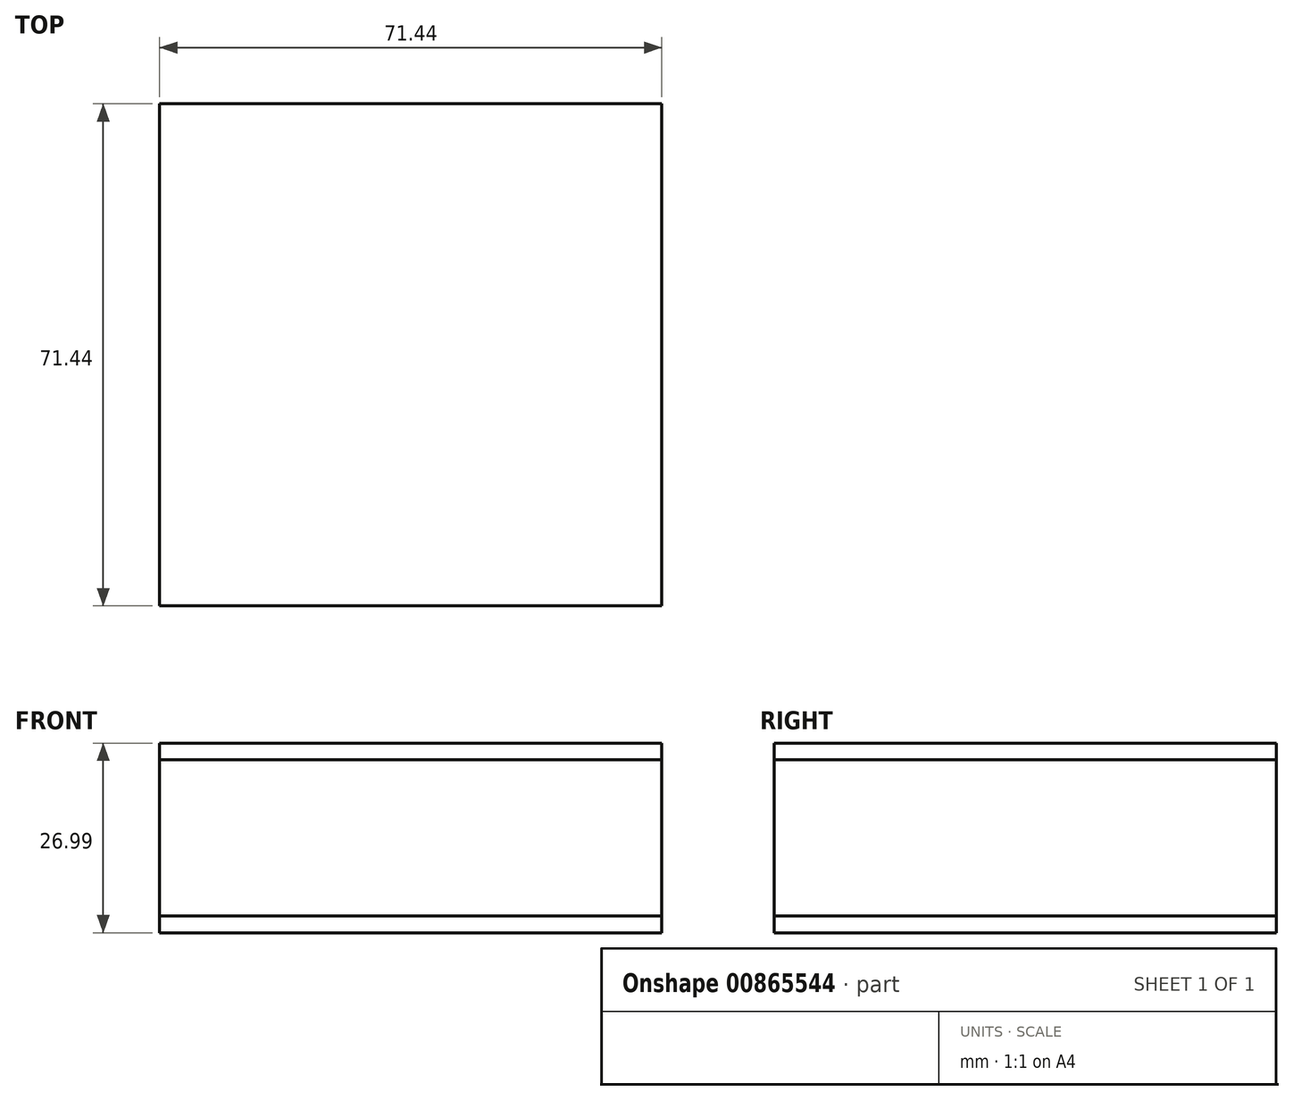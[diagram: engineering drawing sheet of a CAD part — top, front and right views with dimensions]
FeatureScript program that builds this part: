
annotation { "Feature Type Name" : "Feature", "Feature Type Description" : "" }
export const myFeature = defineFeature(function(context is Context, id is Id, definition is map)
    precondition{}
    {
        {
            var Q0;
            Q0=qCreatedBy(makeId("Front.planeOp"),FACE);
            var sketch = newSketch(context, id + "F0", { "sketchPlane" : qUnion([Q0])});
            skLineSegment(sketch, "E0.bottom", {"start": v(0, 0) * mm, "end": v(71.44, 0) * mm});
            skLineSegment(sketch, "E0.top", {"start": v(0, 22.23) * mm, "end": v(71.44, 22.23) * mm});
            skLineSegment(sketch, "E0.left", {"start": v(0, 0) * mm, "end": v(0, 22.23) * mm});
            skLineSegment(sketch, "E0.right", {"start": v(71.44, 0) * mm, "end": v(71.44, 22.23) * mm});
            skSolve(sketch);
        }
        {
            var Q0;
            Q0=makeQuery(id+"F0.imprint","IMPRINT",FACE,{"disambiguationData":[TD([[makeQuery(id+"F0.imprint","IMPRINT",EDGE,{"derivedFrom":sQuery(id+"F0.wireOp",EDGE,"E0.bottom")}),1.0]])]});
            extrude(context, id + "F1", {"entities" : qUnion([Q0]), "depth" : 71.44 * mm, "offsetDistance" : 25.4 * mm});
        }
        {
            var Q0;
            Q0=qCreatedBy(makeId("Front.planeOp"),FACE);
            var sketch = newSketch(context, id + "F2", { "sketchPlane" : qUnion([Q0])});
            skLineSegment(sketch, "E1.bottom", {"start": v(0, 22.23) * mm, "end": v(71.44, 22.23) * mm});
            skLineSegment(sketch, "E1.top", {"start": v(0, 24.6) * mm, "end": v(71.44, 24.6) * mm});
            skLineSegment(sketch, "E1.left", {"start": v(0, 22.23) * mm, "end": v(0, 24.6) * mm});
            skLineSegment(sketch, "E1.right", {"start": v(71.44, 22.23) * mm, "end": v(71.44, 24.6) * mm});
            skLineSegment(sketch, "E2", {"start": v(0, 11.11) * mm, "end": v(71.48, 11.11) * mm, "construction": true});
            skLineSegment(sketch, "E3.MirrorCS", {"start": v(0, 0) * mm, "end": v(71.44, 0) * mm});
            skLineSegment(sketch, "E4.MirrorCS", {"start": v(0, -2.38) * mm, "end": v(71.44, -2.38) * mm});
            skLineSegment(sketch, "E5.MirrorCS", {"start": v(0, 0) * mm, "end": v(0, -2.38) * mm});
            skLineSegment(sketch, "E6.MirrorCS", {"start": v(71.44, 0) * mm, "end": v(71.44, -2.38) * mm});
            skSolve(sketch);
        }
        {
            var Q0;
            Q0=makeQuery(id+"F2.imprint","IMPRINT",FACE,{"disambiguationData":[TD([[makeQuery(id+"F2.imprint","IMPRINT",EDGE,{"derivedFrom":sQuery(id+"F2.wireOp",EDGE,"E1.bottom")}),1.0]])]});
            extrude(context, id + "F3", {"entities" : qUnion([Q0]), "depth" : 71.44 * mm, "offsetDistance" : 25.4 * mm});
        }
        {
            var Q0;
            Q0=makeQuery(id+"F2.imprint","IMPRINT",FACE,{"disambiguationData":[TD([[makeQuery(id+"F2.imprint","IMPRINT",EDGE,{"derivedFrom":sQuery(id+"F2.wireOp",EDGE,"E3.MirrorCS")}),-1.0]])]});
            extrude(context, id + "F4", {"entities" : qUnion([Q0]), "depth" : 71.44 * mm, "offsetDistance" : 25.4 * mm});
        }
    });
